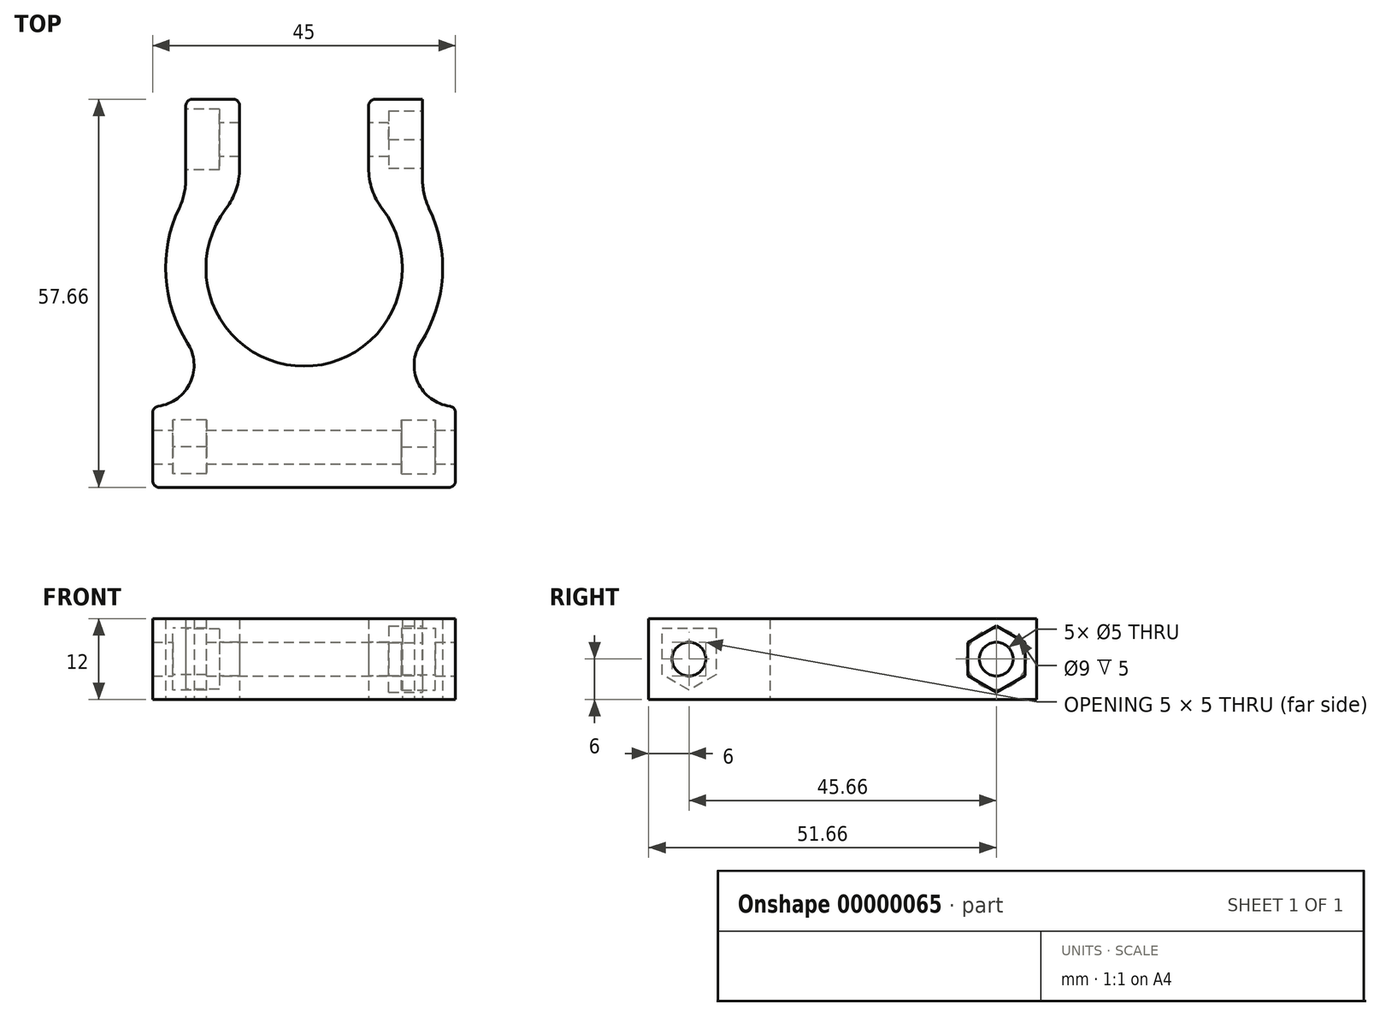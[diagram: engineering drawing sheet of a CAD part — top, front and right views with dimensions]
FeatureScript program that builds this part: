
annotation { "Feature Type Name" : "Feature", "Feature Type Description" : "" }
export const myFeature = defineFeature(function(context is Context, id is Id, definition is map)
    precondition{}
    {
        {
            var Q0;
            Q0=qCreatedBy(makeId("Top.planeOp"),FACE);
            var sketch = newSketch(context, id + "F0", { "sketchPlane" : qUnion([Q0])});
            skArc(sketch, "E0", {"start": v(-9.58, 11) * mm, "mid": v(0, -14.58) * mm, "end": v(9.58, 11) * mm});
            skArc(sketch, "E1", {"start": v(-17.58, 10.7) * mm, "mid": v(0, -20.58) * mm, "end": v(17.58, 10.7) * mm});
            skLineSegment(sketch, "E2", {"start": v(-9.58, 11) * mm, "end": v(-9.58, 25.08) * mm});
            skLineSegment(sketch, "E3", {"start": v(-9.58, 25.08) * mm, "end": v(-17.58, 25.08) * mm});
            skLineSegment(sketch, "E4", {"start": v(-17.58, 25.08) * mm, "end": v(-17.58, 10.7) * mm});
            skLineSegment(sketch, "E5", {"start": v(0, 0) * mm, "end": v(0, 20.58) * mm, "construction": true});
            skLineSegment(sketch, "E6", {"start": v(9.58, 11) * mm, "end": v(9.58, 25.08) * mm});
            skLineSegment(sketch, "E7", {"start": v(9.58, 25.08) * mm, "end": v(17.58, 25.08) * mm});
            skLineSegment(sketch, "E8", {"start": v(17.58, 25.08) * mm, "end": v(17.58, 10.7) * mm});
            skLineSegment(sketch, "E9", {"start": v(-17.58, 19.08) * mm, "end": v(17.58, 19.08) * mm, "construction": true});
            skArc(sketch, "E10", {"start": v(-22.5, -20.58) * mm, "mid": v(-17.1, -17.38) * mm, "end": v(-17.32, -11.11) * mm});
            skLineSegment(sketch, "E11", {"start": v(-22.5, -20.58) * mm, "end": v(-22.5, -32.58) * mm});
            skLineSegment(sketch, "E12", {"start": v(-22.5, -32.58) * mm, "end": v(0, -32.58) * mm});
            skLineSegment(sketch, "E13", {"start": v(-22.5, -20.58) * mm, "end": v(0, -20.58) * mm, "construction": true});
            skArc(sketch, "E14.MirrorCS", {"start": v(22.5, -20.58) * mm, "mid": v(17.1, -17.38) * mm, "end": v(17.32, -11.11) * mm});
            skLineSegment(sketch, "E15.MirrorCS", {"start": v(22.5, -20.58) * mm, "end": v(22.5, -32.58) * mm});
            skLineSegment(sketch, "E16.MirrorCS", {"start": v(22.5, -32.58) * mm, "end": v(0, -32.58) * mm});
            skLineSegment(sketch, "E17", {"start": v(-17.58, 21.58) * mm, "end": v(17.58, 21.58) * mm, "construction": true});
            skLineSegment(sketch, "E18", {"start": v(-17.58, 16.58) * mm, "end": v(17.58, 16.58) * mm, "construction": true});
            skLineSegment(sketch, "E19", {"start": v(0, 16.58) * mm, "end": v(0, 19.08) * mm, "construction": true});
            skLineSegment(sketch, "E20", {"start": v(0, 19.08) * mm, "end": v(0, 21.58) * mm, "construction": true});
            skLineSegment(sketch, "E21", {"start": v(-9.58, 11) * mm, "end": v(9.58, 11) * mm, "construction": true});
            skLineSegment(sketch, "E22", {"start": v(-12.58, 25.08) * mm, "end": v(-12.58, 7.37) * mm, "construction": true});
            skArc(sketch, "E23", {"start": v(9.58, 11) * mm, "mid": v(0, 14.58) * mm, "end": v(-9.58, 11) * mm, "construction": true});
            skLineSegment(sketch, "E24.MirrorCS", {"start": v(12.58, 25.08) * mm, "end": v(12.58, 7.37) * mm, "construction": true});
            skSolve(sketch);
        }
        {
            var Q0;
            {var subQ1=sQuery(id+"F0.wireOp",EDGE,"E10");Q0=makeQuery(id+"F0.imprint","IMPRINT",FACE,{"disambiguationData":[TD([[makeQuery(id+"F0.imprint","IMPRINT",EDGE,{"derivedFrom":subQ1}),-1.0]])]});}
            var Q1;
            Q1=makeQuery(id+"F0.imprint","IMPRINT",FACE,{"disambiguationData":[TD([[makeQuery(id+"F0.imprint","IMPRINT",EDGE,{"derivedFrom":sQuery(id+"F0.wireOp",EDGE,"E0")}),-1.0]])]});
            extrude(context, id + "F1", {"entities" : qUnion([Q0, Q1]), "depth" : 12 * mm, "symmetric" : true});
        }
        {
            var Q0;
            Q0=makeQuery(id+"F1.opExtrude","SWEPT_FACE",FACE,{"disambiguationData":[OSD([sQuery(id+"F0.wireOp",EDGE,"E4")])]});
            var sketch = newSketch(context, id + "F2", { "sketchPlane" : qUnion([Q0])});
            skPoint(sketch, "E25", {"position": v(-19.08, 0) * mm});
            skSolve(sketch);
        }
        {
            var Q0;
            Q0=sQuery(id+"F2.wireOp",VERTEX,"E25");
            var Q1;
            Q1=makeQuery(id+"F1.opExtrude","SWEPT_BODY",BODY,{"disambiguationData":[OSD([sQuery(id+"F0.wireOp",EDGE,"E0"),sQuery(id+"F0.wireOp",EDGE,"E1"),sQuery(id+"F0.wireOp",EDGE,"E2"),sQuery(id+"F0.wireOp",EDGE,"E3"),sQuery(id+"F0.wireOp",EDGE,"E4"),sQuery(id+"F0.wireOp",EDGE,"E6"),sQuery(id+"F0.wireOp",EDGE,"E7"),sQuery(id+"F0.wireOp",EDGE,"E8"),sQuery(id+"F0.wireOp",EDGE,"E10"),sQuery(id+"F0.wireOp",EDGE,"E11"),sQuery(id+"F0.wireOp",EDGE,"E12"),sQuery(id+"F0.wireOp",EDGE,"E14.MirrorCS"),sQuery(id+"F0.wireOp",EDGE,"E15.MirrorCS"),sQuery(id+"F0.wireOp",EDGE,"E16.MirrorCS")])]});
            hole(context, id + "F3", {"style" : HoleStyle.C_BORE, "holeDiameter" : 5 * mm, "cBoreDiameter" : 9 * mm, "cBoreDepth" : 5 * mm, "endStyle" : HoleEndStyle.THROUGH, "locations" : qUnion([Q0]), "scope" : qUnion([Q1])});
        }
        {
            var Q0;
            Q0=makeQuery(id+"F1.opExtrude","SWEPT_FACE",FACE,{"disambiguationData":[OSD([sQuery(id+"F0.wireOp",EDGE,"E8")])]});
            var sketch = newSketch(context, id + "F4", { "sketchPlane" : qUnion([Q0])});
            skCircle(sketch, "E26.cCircle", {"center": v(19.08, 0) * mm, "radius": 4.25 * mm, "construction": true});
            skLineSegment(sketch, "E26.0", {"start": v(19.08, -4.9) * mm, "end": v(14.83, -2.45) * mm});
            skLineSegment(sketch, "E26.1", {"start": v(14.83, -2.45) * mm, "end": v(14.83, 2.45) * mm});
            skLineSegment(sketch, "E26.2", {"start": v(14.83, 2.45) * mm, "end": v(19.08, 4.9) * mm});
            skLineSegment(sketch, "E26.3", {"start": v(19.08, 4.9) * mm, "end": v(23.33, 2.45) * mm});
            skLineSegment(sketch, "E26.4", {"start": v(23.33, 2.45) * mm, "end": v(23.33, -2.45) * mm});
            skLineSegment(sketch, "E26.5", {"start": v(23.33, -2.45) * mm, "end": v(19.08, -4.9) * mm});
            skPoint(sketch, "E26.0.midPoint", {"position": v(16.95, -3.68) * mm});
            skSolve(sketch);
        }
        {
            var Q0;
            Q0=makeQuery(id+"F4.imprint","IMPRINT",FACE,{"disambiguationData":[TD([[makeQuery(id+"F4.imprint","IMPRINT",EDGE,{"derivedFrom":sQuery(id+"F4.wireOp",EDGE,"E26.0")}),-1.0]])]});
            extrude(context, id + "F5", {"entities" : qUnion([Q0]), "operationType" : NewBodyOperationType.REMOVE, "oppositeDirection" : true, "depth" : 5 * mm});
        }
        {
            var Q0;
            Q0=makeQuery(id+"F1.opExtrude","SWEPT_FACE",FACE,{"disambiguationData":[OSD([sQuery(id+"F0.wireOp",EDGE,"E15.MirrorCS")])]});
            var sketch = newSketch(context, id + "F6", { "sketchPlane" : qUnion([Q0])});
            skCircle(sketch, "E27.cCircle", {"center": v(-26.58, 0) * mm, "radius": 4 * mm, "construction": true});
            skLineSegment(sketch, "E27.0", {"start": v(-30.58, 2.3) * mm, "end": v(-26.58, 4.62) * mm});
            skLineSegment(sketch, "E27.1", {"start": v(-26.58, 4.62) * mm, "end": v(-22.58, 2.3) * mm});
            skLineSegment(sketch, "E27.2", {"start": v(-22.58, 2.3) * mm, "end": v(-22.58, -2.3) * mm});
            skLineSegment(sketch, "E27.3", {"start": v(-22.58, -2.3) * mm, "end": v(-26.58, -4.62) * mm});
            skLineSegment(sketch, "E27.4", {"start": v(-26.58, -4.62) * mm, "end": v(-30.58, -2.3) * mm});
            skLineSegment(sketch, "E27.5", {"start": v(-30.58, -2.3) * mm, "end": v(-30.58, 2.3) * mm});
            skPoint(sketch, "E27.0.midPoint", {"position": v(-28.58, 3.46) * mm});
            skLineSegment(sketch, "E28", {"start": v(-32.58, 0) * mm, "end": v(-20.58, 0) * mm, "construction": true});
            skLineSegment(sketch, "E29", {"start": v(-30.58, 2.3) * mm, "end": v(-30.58, 4.62) * mm});
            skLineSegment(sketch, "E30", {"start": v(-30.58, 4.62) * mm, "end": v(-26.58, 4.62) * mm});
            skLineSegment(sketch, "E31", {"start": v(-22.58, 2.3) * mm, "end": v(-22.58, 4.62) * mm});
            skLineSegment(sketch, "E32", {"start": v(-22.58, 4.62) * mm, "end": v(-26.58, 4.62) * mm});
            skSolve(sketch);
        }
        {
            var Q0;
            Q0=makeQuery(id+"F6.imprint","IMPRINT",FACE,{"disambiguationData":[TD([[makeQuery(id+"F6.imprint","IMPRINT",EDGE,{"derivedFrom":sQuery(id+"F6.wireOp",EDGE,"E27.0")}),-1.0]])]});
            var Q1;
            Q1=makeQuery(id+"F6.imprint","IMPRINT",FACE,{"disambiguationData":[TD([[makeQuery(id+"F6.imprint","IMPRINT",EDGE,{"derivedFrom":sQuery(id+"F6.wireOp",EDGE,"E27.0")}),1.0]])]});
            var Q2;
            Q2=makeQuery(id+"F6.imprint","IMPRINT",FACE,{"disambiguationData":[TD([[makeQuery(id+"F6.imprint","IMPRINT",EDGE,{"derivedFrom":sQuery(id+"F6.wireOp",EDGE,"E27.1")}),1.0]])]});
            extrude(context, id + "F7", {"entities" : qUnion([Q0, Q1, Q2]), "operationType" : NewBodyOperationType.REMOVE, "oppositeDirection" : true, "depth" : 8 * mm, "hasSecondDirection" : true, "secondDirectionOppositeDirection" : true, "secondDirectionDepth" : 3 * mm});
        }
        {
            var Q0;
            Q0=makeQuery(id+"F7.boolean.opBoolean","COPY",FACE,{"derivedFrom":makeQuery(id+"F7.opExtrude","CAP_FACE",FACE,{"disambiguationData":[OSD([sQuery(id+"F6.wireOp",EDGE,"E27.2"),sQuery(id+"F6.wireOp",EDGE,"E27.3"),sQuery(id+"F6.wireOp",EDGE,"E27.4"),sQuery(id+"F6.wireOp",EDGE,"E27.5"),sQuery(id+"F6.wireOp",EDGE,"E29"),sQuery(id+"F6.wireOp",EDGE,"E30"),sQuery(id+"F6.wireOp",EDGE,"E31"),sQuery(id+"F6.wireOp",EDGE,"E32")])],"isStart":false})});
            var Q1;
            Q1=makeQuery(id+"F7.boolean.opBoolean","COPY",FACE,{"derivedFrom":makeQuery(id+"F7.opExtrude","CAP_FACE",FACE,{"disambiguationData":[OSD([sQuery(id+"F6.wireOp",EDGE,"E27.2"),sQuery(id+"F6.wireOp",EDGE,"E27.3"),sQuery(id+"F6.wireOp",EDGE,"E27.4"),sQuery(id+"F6.wireOp",EDGE,"E27.5"),sQuery(id+"F6.wireOp",EDGE,"E29"),sQuery(id+"F6.wireOp",EDGE,"E30"),sQuery(id+"F6.wireOp",EDGE,"E31"),sQuery(id+"F6.wireOp",EDGE,"E32")])],"isStart":true})});
            var Q2;
            Q2=makeQuery(id+"F7.boolean.opBoolean","COPY",FACE,{"derivedFrom":makeQuery(id+"F7.opExtrude","SWEPT_FACE",FACE,{"disambiguationData":[OSD([sQuery(id+"F6.wireOp",EDGE,"E27.4")])]})});
            var Q3;
            Q3=makeQuery(id+"F7.boolean.opBoolean","COPY",FACE,{"derivedFrom":makeQuery(id+"F7.opExtrude","SWEPT_FACE",FACE,{"disambiguationData":[OSD([sQuery(id+"F6.wireOp",EDGE,"E27.2"),sQuery(id+"F6.wireOp",EDGE,"E31")])]})});
            var Q4;
            Q4=makeQuery(id+"F7.boolean.opBoolean","COPY",FACE,{"derivedFrom":makeQuery(id+"F7.opExtrude","SWEPT_FACE",FACE,{"disambiguationData":[OSD([sQuery(id+"F6.wireOp",EDGE,"E27.3")])]})});
            var Q5;
            Q5=makeQuery(id+"F7.boolean.opBoolean","COPY",FACE,{"derivedFrom":makeQuery(id+"F7.opExtrude","SWEPT_FACE",FACE,{"disambiguationData":[OSD([sQuery(id+"F6.wireOp",EDGE,"E27.5"),sQuery(id+"F6.wireOp",EDGE,"E29")])]})});
            var Q6;
            Q6=makeQuery(id+"F7.boolean.opBoolean","COPY",FACE,{"derivedFrom":makeQuery(id+"F7.opExtrude","SWEPT_FACE",FACE,{"disambiguationData":[OSD([sQuery(id+"F6.wireOp",EDGE,"E30"),sQuery(id+"F6.wireOp",EDGE,"E32")])]})});
            var Q7;
            Q7=qCreatedBy(makeId("Right.planeOp"),FACE);
            mirror(context, id + "F8", {"faces" : qUnion([Q0, Q1, Q2, Q3, Q4, Q5, Q6]), "mirrorPlane" : qUnion([Q7]), "patternType" : MirrorType.FACE});
        }
        {
            var Q0;
            Q0=sQuery(id+"F6.wireOp",VERTEX,"E27.cCircle.center");
            var Q1;
            Q1=makeQuery(id+"F1.opExtrude","SWEPT_BODY",BODY,{"disambiguationData":[OSD([sQuery(id+"F0.wireOp",EDGE,"E0"),sQuery(id+"F0.wireOp",EDGE,"E1"),sQuery(id+"F0.wireOp",EDGE,"E2"),sQuery(id+"F0.wireOp",EDGE,"E3"),sQuery(id+"F0.wireOp",EDGE,"E4"),sQuery(id+"F0.wireOp",EDGE,"E6"),sQuery(id+"F0.wireOp",EDGE,"E7"),sQuery(id+"F0.wireOp",EDGE,"E8"),sQuery(id+"F0.wireOp",EDGE,"E10"),sQuery(id+"F0.wireOp",EDGE,"E11"),sQuery(id+"F0.wireOp",EDGE,"E12"),sQuery(id+"F0.wireOp",EDGE,"E14.MirrorCS"),sQuery(id+"F0.wireOp",EDGE,"E15.MirrorCS"),sQuery(id+"F0.wireOp",EDGE,"E16.MirrorCS")])]});
            hole(context, id + "F9", {"style" : HoleStyle.SIMPLE, "holeDiameter" : 5 * mm, "endStyle" : HoleEndStyle.THROUGH, "locations" : qUnion([Q0]), "scope" : qUnion([Q1])});
        }
        {
            var Q0;
            Q0=makeQuery(id+"F1.opExtrude","SWEPT_EDGE",EDGE,{"disambiguationData":[OSD([sQuery(id+"F0.wireOp",EDGE,"E0"),sQuery(id+"F0.wireOp",EDGE,"E2")])]});
            var Q1;
            Q1=makeQuery(id+"F1.opExtrude","SWEPT_EDGE",EDGE,{"disambiguationData":[OSD([sQuery(id+"F0.wireOp",EDGE,"E0"),sQuery(id+"F0.wireOp",EDGE,"E6")])]});
            var Q2;
            Q2=makeQuery(id+"F1.opExtrude","SWEPT_EDGE",EDGE,{"disambiguationData":[OSD([sQuery(id+"F0.wireOp",EDGE,"E1"),sQuery(id+"F0.wireOp",EDGE,"E4")])]});
            var Q3;
            Q3=makeQuery(id+"F1.opExtrude","SWEPT_EDGE",EDGE,{"disambiguationData":[OSD([sQuery(id+"F0.wireOp",EDGE,"E1"),sQuery(id+"F0.wireOp",EDGE,"E8")])]});
            fillet(context, id + "F10", {"entities" : qUnion([Q0, Q1, Q2, Q3]), "radius" : 10 * mm, "tangentPropagation" : true, "allowEdgeOverflow" : false});
        }
        {
            var Q0;
            Q0=makeQuery(id+"F1.opExtrude","SWEPT_EDGE",EDGE,{"disambiguationData":[OSD([sQuery(id+"F0.wireOp",EDGE,"E2"),sQuery(id+"F0.wireOp",EDGE,"E3")])]});
            var Q1;
            Q1=makeQuery(id+"F1.opExtrude","SWEPT_EDGE",EDGE,{"disambiguationData":[OSD([sQuery(id+"F0.wireOp",EDGE,"E6"),sQuery(id+"F0.wireOp",EDGE,"E7")])]});
            var Q2;
            Q2=makeQuery(id+"F1.opExtrude","SWEPT_EDGE",EDGE,{"disambiguationData":[OSD([sQuery(id+"F0.wireOp",EDGE,"E3"),sQuery(id+"F0.wireOp",EDGE,"E4")])]});
            var Q3;
            Q3=makeQuery(id+"F1.opExtrude","SWEPT_EDGE",EDGE,{"disambiguationData":[OSD([sQuery(id+"F0.wireOp",EDGE,"E10"),sQuery(id+"F0.wireOp",EDGE,"E11")])]});
            var Q4;
            Q4=makeQuery(id+"F1.opExtrude","SWEPT_EDGE",EDGE,{"disambiguationData":[OSD([sQuery(id+"F0.wireOp",EDGE,"E11"),sQuery(id+"F0.wireOp",EDGE,"E12")])]});
            var Q5;
            Q5=makeQuery(id+"F1.opExtrude","SWEPT_EDGE",EDGE,{"disambiguationData":[OSD([sQuery(id+"F0.wireOp",EDGE,"E15.MirrorCS"),sQuery(id+"F0.wireOp",EDGE,"E16.MirrorCS")])]});
            var Q6;
            Q6=makeQuery(id+"F1.opExtrude","SWEPT_EDGE",EDGE,{"disambiguationData":[OSD([sQuery(id+"F0.wireOp",EDGE,"E14.MirrorCS"),sQuery(id+"F0.wireOp",EDGE,"E15.MirrorCS")])]});
            fillet(context, id + "F11", {"entities" : qUnion([Q0, Q1, Q2, Q3, Q4, Q5, Q6]), "radius" : 1 * mm, "tangentPropagation" : true, "allowEdgeOverflow" : false});
        }
    });
